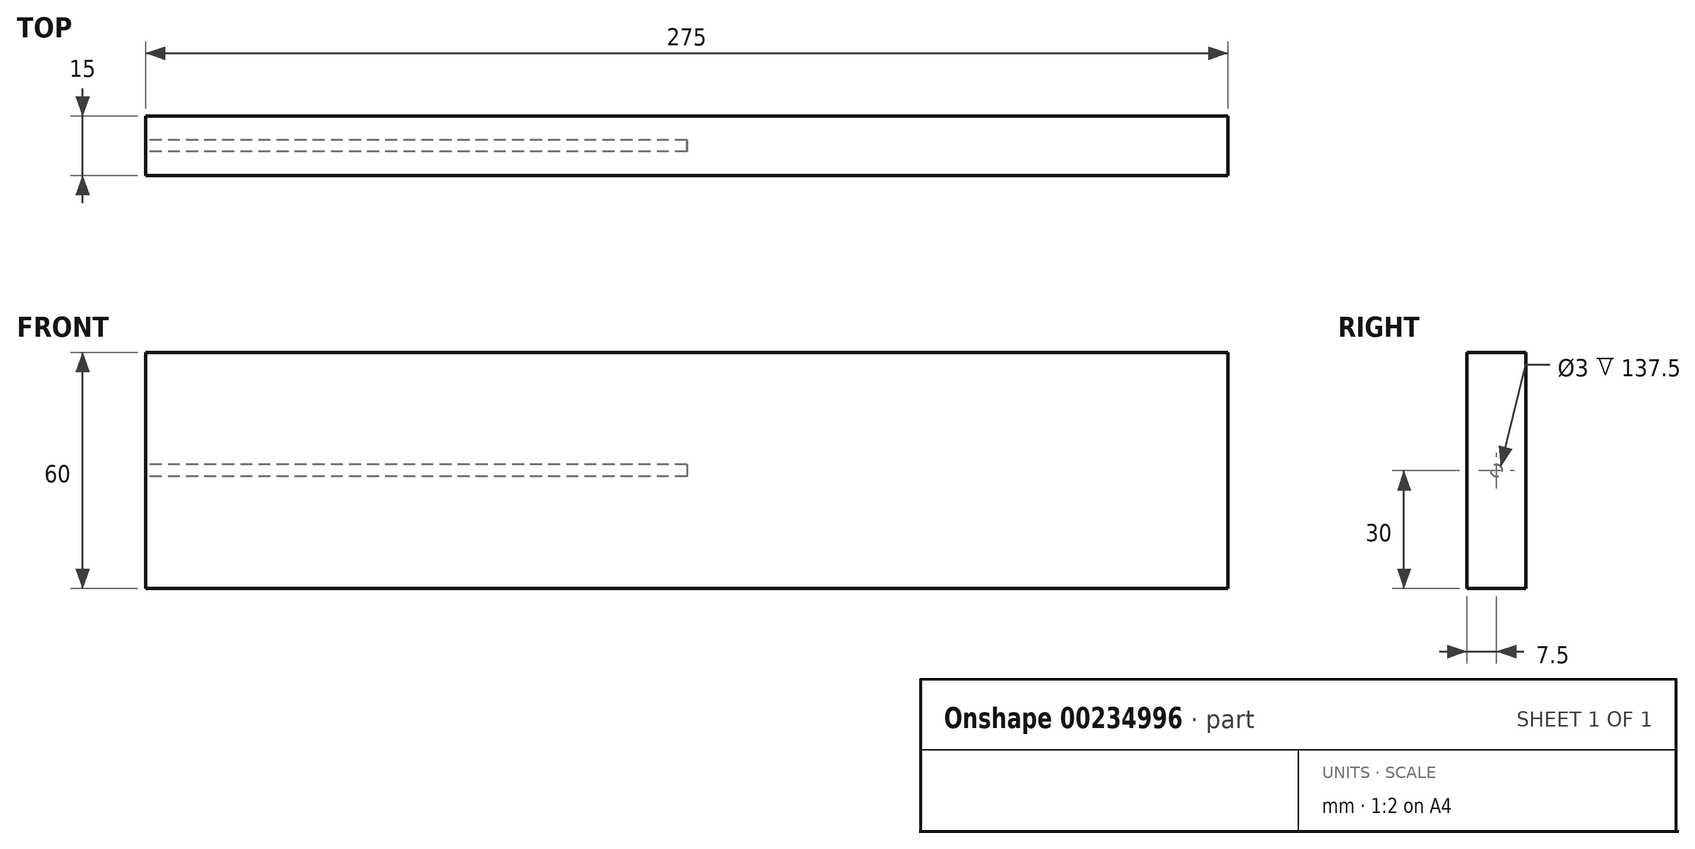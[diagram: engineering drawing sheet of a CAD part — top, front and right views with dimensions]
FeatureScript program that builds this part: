
annotation { "Feature Type Name" : "Feature", "Feature Type Description" : "" }
export const myFeature = defineFeature(function(context is Context, id is Id, definition is map)
    precondition{}
    {
        {
            var Q0;
            Q0=qCreatedBy(makeId("Front.planeOp"),FACE);
            var sketch = newSketch(context, id + "F0", { "sketchPlane" : qUnion([Q0])});
            skLineSegment(sketch, "E0.bottom", {"start": v(137.5, -30) * mm, "end": v(-137.5, -30) * mm});
            skLineSegment(sketch, "E0.top", {"start": v(137.5, 30) * mm, "end": v(-137.5, 30) * mm});
            skLineSegment(sketch, "E0.left", {"start": v(137.5, -30) * mm, "end": v(137.5, 30) * mm});
            skLineSegment(sketch, "E0.right", {"start": v(-137.5, -30) * mm, "end": v(-137.5, 30) * mm});
            skPoint(sketch, "E0.middle", {"position": v(0, 0) * mm});
            skSolve(sketch);
        }
        {
            var Q0;
            Q0=qSketchRegion(id+"F0",true);
            extrude(context, id + "F1", {"entities" : qUnion([Q0]), "endBound" : BoundingType.SYMMETRIC, "depth" : 15 * mm});
        }
        {
            var Q0;
            Q0=makeQuery(id+"F1.opExtrude","SWEPT_FACE",FACE,{"disambiguationData":[OSD([sQuery(id+"F0.wireOp",EDGE,"E0.right")])]});
            var sketch = newSketch(context, id + "F2", { "sketchPlane" : qUnion([Q0])});
            skCircle(sketch, "E1", {"center": v(0, 0) * mm, "radius": 1.5 * mm});
            skSolve(sketch);
        }
        {
            var Q0;
            Q0=qSketchRegion(id+"F2",true);
            extrude(context, id + "F3", {"entities" : qUnion([Q0]), "operationType" : NewBodyOperationType.REMOVE, "oppositeDirection" : true, "depth" : (275 / 2) * mm});
        }
    });
